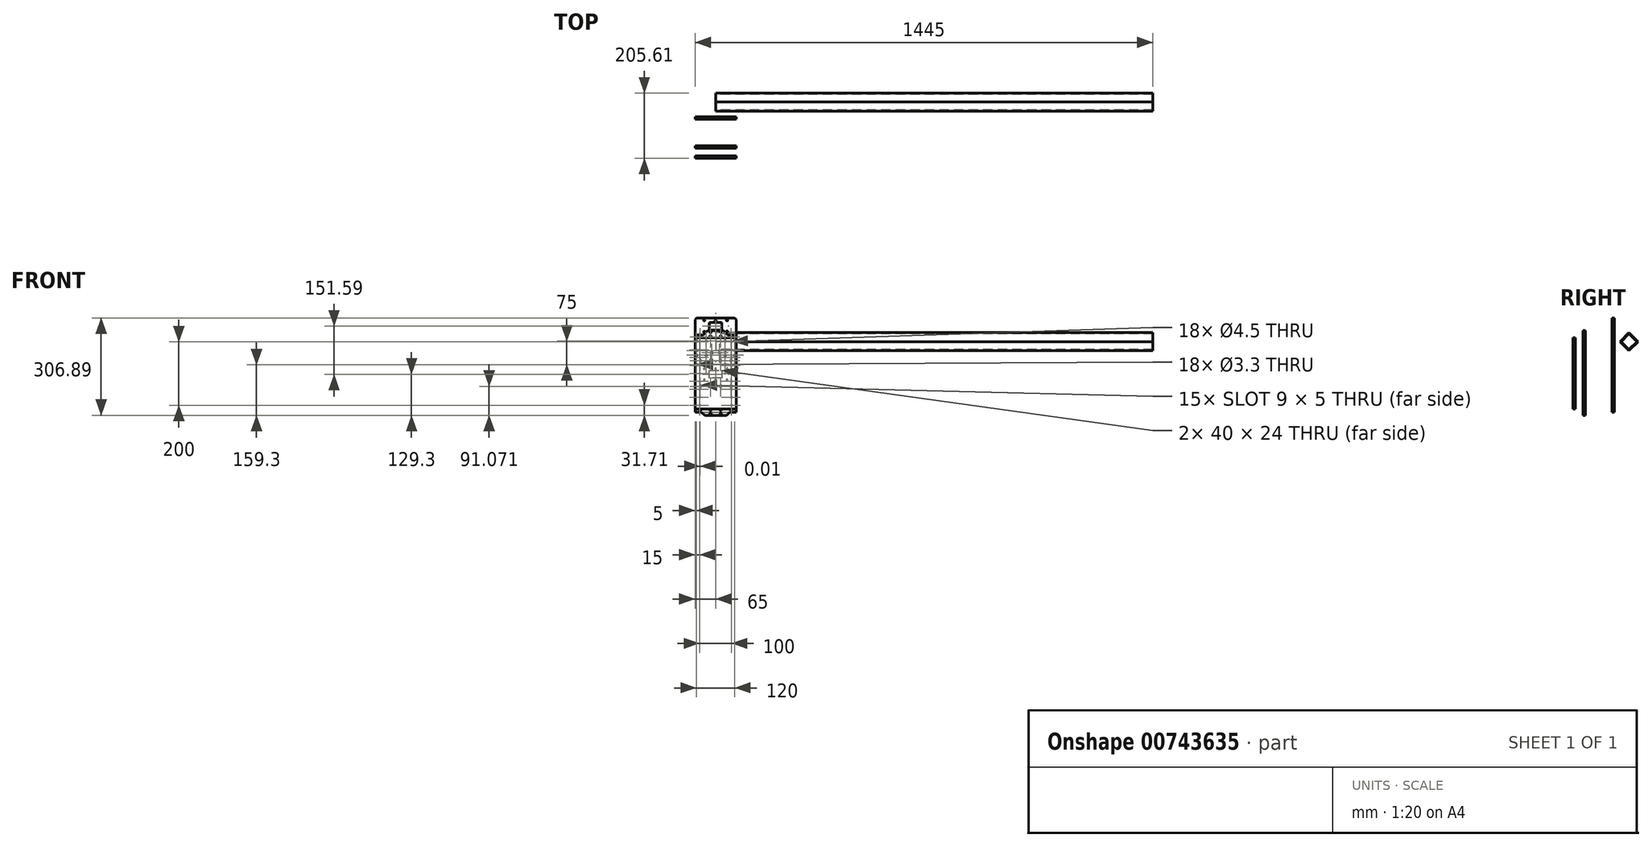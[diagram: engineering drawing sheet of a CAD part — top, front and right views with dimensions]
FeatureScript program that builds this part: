
annotation { "Feature Type Name" : "Feature", "Feature Type Description" : "" }
export const myFeature = defineFeature(function(context is Context, id is Id, definition is map)
    precondition{}
    {
        {
            var Q0;
            Q0=qCreatedBy(makeId("Front.planeOp"),FACE);
            var sketch = newSketch(context, id + "F0", { "sketchPlane" : qUnion([Q0])});
            skLineSegment(sketch, "E0", {"start": v(20, -14.5) * mm, "end": v(-20, -14.5) * mm});
            skLineSegment(sketch, "E1", {"start": v(20, 9.5) * mm, "end": v(20, -14.5) * mm});
            skLineSegment(sketch, "E2", {"start": v(-20, 9.5) * mm, "end": v(20, 9.5) * mm});
            skLineSegment(sketch, "E3", {"start": v(-20, -14.5) * mm, "end": v(-20, 9.5) * mm});
            skLineSegment(sketch, "E4", {"start": v(-51, 50.32) * mm, "end": v(-51, 47.32) * mm});
            skLineSegment(sketch, "E5", {"start": v(-46.01, 47.32) * mm, "end": v(-46.01, 50.32) * mm});
            skLineSegment(sketch, "E6", {"start": v(-18.67, 50.32) * mm, "end": v(-18.67, 47.32) * mm});
            skLineSegment(sketch, "E7", {"start": v(-13.67, 47.32) * mm, "end": v(-13.67, 50.32) * mm});
            skLineSegment(sketch, "E8", {"start": v(13.67, 50.32) * mm, "end": v(13.67, 47.32) * mm});
            skLineSegment(sketch, "E9", {"start": v(18.67, 47.32) * mm, "end": v(18.67, 50.32) * mm});
            skLineSegment(sketch, "E10", {"start": v(46, 50.32) * mm, "end": v(46, 47.32) * mm});
            skLineSegment(sketch, "E11", {"start": v(51, 47.32) * mm, "end": v(51, 50.32) * mm});
            skLineSegment(sketch, "E12", {"start": v(-51, 103.5) * mm, "end": v(-51, 100.5) * mm});
            skLineSegment(sketch, "E13", {"start": v(-46.01, 100.5) * mm, "end": v(-46.01, 103.5) * mm});
            skLineSegment(sketch, "E14", {"start": v(-13.67, 100.5) * mm, "end": v(-13.67, 103.5) * mm});
            skLineSegment(sketch, "E15", {"start": v(-18.67, 103.5) * mm, "end": v(-18.67, 100.5) * mm});
            skLineSegment(sketch, "E16", {"start": v(18.67, 100.5) * mm, "end": v(18.67, 103.5) * mm});
            skLineSegment(sketch, "E17", {"start": v(13.67, 103.5) * mm, "end": v(13.67, 100.5) * mm});
            skLineSegment(sketch, "E18", {"start": v(51, 100.5) * mm, "end": v(51, 103.5) * mm});
            skLineSegment(sketch, "E19", {"start": v(46, 103.5) * mm, "end": v(46, 100.5) * mm});
            skLineSegment(sketch, "E20", {"start": v(-46.01, -55.32) * mm, "end": v(-46.01, -52.32) * mm});
            skLineSegment(sketch, "E21", {"start": v(-51, -52.32) * mm, "end": v(-51, -55.32) * mm});
            skLineSegment(sketch, "E22", {"start": v(-13.67, -55.32) * mm, "end": v(-13.67, -52.32) * mm});
            skLineSegment(sketch, "E23", {"start": v(-18.67, -52.32) * mm, "end": v(-18.67, -55.32) * mm});
            skLineSegment(sketch, "E24", {"start": v(18.67, -55.32) * mm, "end": v(18.67, -52.32) * mm});
            skLineSegment(sketch, "E25", {"start": v(13.67, -52.32) * mm, "end": v(13.67, -55.32) * mm});
            skLineSegment(sketch, "E26", {"start": v(51, -55.32) * mm, "end": v(51, -52.32) * mm});
            skLineSegment(sketch, "E27", {"start": v(46, -52.32) * mm, "end": v(46, -55.32) * mm});
            skLineSegment(sketch, "E28", {"start": v(60, -113.5) * mm, "end": v(65, -108.5) * mm});
            skLineSegment(sketch, "E29", {"start": v(34, -124.5) * mm, "end": v(45, -113.5) * mm});
            skLineSegment(sketch, "E30", {"start": v(34, -124.5) * mm, "end": v(-34, -124.5) * mm});
            skLineSegment(sketch, "E31", {"start": v(-45, -113.5) * mm, "end": v(-34, -124.5) * mm});
            skLineSegment(sketch, "E32", {"start": v(-65, -108.5) * mm, "end": v(-60, -113.5) * mm});
            skLineSegment(sketch, "E33", {"start": v(-60, 110.5) * mm, "end": v(-65, 105.5) * mm});
            skLineSegment(sketch, "E34", {"start": v(-39, 110.5) * mm, "end": v(-60, 110.5) * mm});
            skLineSegment(sketch, "E35", {"start": v(-25, 124.5) * mm, "end": v(-39, 110.5) * mm});
            skLineSegment(sketch, "E36", {"start": v(-25, 124.5) * mm, "end": v(25, 124.5) * mm});
            skLineSegment(sketch, "E37", {"start": v(39, 110.5) * mm, "end": v(25, 124.5) * mm});
            skLineSegment(sketch, "E38", {"start": v(60, 110.5) * mm, "end": v(39, 110.5) * mm});
            skLineSegment(sketch, "E39", {"start": v(65, 105.5) * mm, "end": v(60, 110.5) * mm});
            skLineSegment(sketch, "E40", {"start": v(-65, 105.5) * mm, "end": v(-65, -108.5) * mm});
            skLineSegment(sketch, "E41", {"start": v(65, -108.5) * mm, "end": v(65, 105.5) * mm});
            skLineSegment(sketch, "E42", {"start": v(45, -113.5) * mm, "end": v(60, -113.5) * mm});
            skLineSegment(sketch, "E43", {"start": v(-60, -113.5) * mm, "end": v(-45, -113.5) * mm});
            skCircle(sketch, "E44", {"center": v(-48.5, -107) * mm, "radius": 2.5 * mm});
            skCircle(sketch, "E45", {"center": v(-16.17, -107) * mm, "radius": 2.5 * mm});
            skCircle(sketch, "E46", {"center": v(16.17, -107) * mm, "radius": 2.5 * mm});
            skCircle(sketch, "E47", {"center": v(48.5, -107) * mm, "radius": 2.5 * mm});
            skCircle(sketch, "E48", {"center": v(-36, 15) * mm, "radius": 2.05 * mm});
            skCircle(sketch, "E49", {"center": v(0, 15) * mm, "radius": 2.05 * mm});
            skCircle(sketch, "E50", {"center": v(36, 15) * mm, "radius": 2.05 * mm});
            skCircle(sketch, "E51", {"center": v(36, -20) * mm, "radius": 2.05 * mm});
            skCircle(sketch, "E52", {"center": v(0, -20) * mm, "radius": 2.05 * mm});
            skCircle(sketch, "E53", {"center": v(-36, -20) * mm, "radius": 2.05 * mm});
            skCircle(sketch, "E54", {"center": v(0, 119) * mm, "radius": 2.05 * mm});
            skCircle(sketch, "E55", {"center": v(16.17, -119.5) * mm, "radius": 2.5 * mm});
            skCircle(sketch, "E56", {"center": v(-16.17, -119.5) * mm, "radius": 2.5 * mm});
            skCircle(sketch, "E57", {"center": v(16.17, 119) * mm, "radius": 2.5 * mm});
            skCircle(sketch, "E58", {"center": v(-16.17, 119) * mm, "radius": 2.5 * mm});
            skCircle(sketch, "E59", {"center": v(50, -90) * mm, "radius": 2.25 * mm});
            skCircle(sketch, "E60", {"center": v(50, -65) * mm, "radius": 2.25 * mm});
            skCircle(sketch, "E61", {"center": v(-50, -90) * mm, "radius": 2.25 * mm});
            skCircle(sketch, "E62", {"center": v(-50, -65) * mm, "radius": 2.25 * mm});
            skCircle(sketch, "E63", {"center": v(-50, -40) * mm, "radius": 2.25 * mm});
            skCircle(sketch, "E64", {"center": v(-50, -15) * mm, "radius": 2.25 * mm});
            skCircle(sketch, "E65", {"center": v(50, -40) * mm, "radius": 2.25 * mm});
            skCircle(sketch, "E66", {"center": v(50, -15) * mm, "radius": 2.25 * mm});
            skCircle(sketch, "E67", {"center": v(50, 10) * mm, "radius": 2.25 * mm});
            skCircle(sketch, "E68", {"center": v(-50, 10) * mm, "radius": 2.25 * mm});
            skCircle(sketch, "E69", {"center": v(-50, 35) * mm, "radius": 2.25 * mm});
            skCircle(sketch, "E70", {"center": v(50, 35) * mm, "radius": 2.25 * mm});
            skCircle(sketch, "E71", {"center": v(50, 60) * mm, "radius": 2.25 * mm});
            skCircle(sketch, "E72", {"center": v(-50, 60) * mm, "radius": 2.25 * mm});
            skCircle(sketch, "E73", {"center": v(-50, 85) * mm, "radius": 2.25 * mm});
            skCircle(sketch, "E74", {"center": v(50, 85) * mm, "radius": 2.25 * mm});
            skArc(sketch, "E75", {"start": v(-51, 47.32) * mm, "mid": v(-48.5, 44.82) * mm, "end": v(-46, 47.32) * mm});
            skArc(sketch, "E76", {"start": v(-46, 50.32) * mm, "mid": v(-48.5, 52.82) * mm, "end": v(-51, 50.32) * mm});
            skArc(sketch, "E77", {"start": v(-18.67, 47.32) * mm, "mid": v(-16.17, 44.82) * mm, "end": v(-13.67, 47.32) * mm});
            skArc(sketch, "E78", {"start": v(-13.67, 50.32) * mm, "mid": v(-16.17, 52.82) * mm, "end": v(-18.67, 50.32) * mm});
            skArc(sketch, "E79", {"start": v(13.67, 47.32) * mm, "mid": v(16.17, 44.82) * mm, "end": v(18.67, 47.32) * mm});
            skArc(sketch, "E80", {"start": v(18.67, 50.32) * mm, "mid": v(16.17, 52.82) * mm, "end": v(13.67, 50.32) * mm});
            skArc(sketch, "E81", {"start": v(46, 47.32) * mm, "mid": v(48.5, 44.82) * mm, "end": v(51, 47.32) * mm});
            skArc(sketch, "E82", {"start": v(51, 50.32) * mm, "mid": v(48.5, 52.82) * mm, "end": v(46, 50.32) * mm});
            skArc(sketch, "E83", {"start": v(-51, 100.5) * mm, "mid": v(-48.5, 98) * mm, "end": v(-46, 100.5) * mm});
            skArc(sketch, "E84", {"start": v(-46, 103.5) * mm, "mid": v(-48.5, 106) * mm, "end": v(-51, 103.5) * mm});
            skArc(sketch, "E85", {"start": v(-18.67, 100.5) * mm, "mid": v(-16.17, 98) * mm, "end": v(-13.67, 100.5) * mm});
            skArc(sketch, "E86", {"start": v(-13.67, 103.5) * mm, "mid": v(-16.17, 106) * mm, "end": v(-18.67, 103.5) * mm});
            skArc(sketch, "E87", {"start": v(13.67, 100.5) * mm, "mid": v(16.17, 98) * mm, "end": v(18.67, 100.5) * mm});
            skArc(sketch, "E88", {"start": v(18.67, 103.5) * mm, "mid": v(16.17, 106) * mm, "end": v(13.67, 103.5) * mm});
            skArc(sketch, "E89", {"start": v(46, 100.5) * mm, "mid": v(48.5, 98) * mm, "end": v(51, 100.5) * mm});
            skArc(sketch, "E90", {"start": v(51, 103.5) * mm, "mid": v(48.5, 106) * mm, "end": v(46, 103.5) * mm});
            skArc(sketch, "E91", {"start": v(-51, -55.32) * mm, "mid": v(-48.5, -57.82) * mm, "end": v(-46, -55.32) * mm});
            skArc(sketch, "E92", {"start": v(-46, -52.32) * mm, "mid": v(-48.5, -49.82) * mm, "end": v(-51, -52.32) * mm});
            skArc(sketch, "E93", {"start": v(-18.67, -55.32) * mm, "mid": v(-16.17, -57.82) * mm, "end": v(-13.67, -55.32) * mm});
            skArc(sketch, "E94", {"start": v(-13.67, -52.32) * mm, "mid": v(-16.17, -49.82) * mm, "end": v(-18.67, -52.32) * mm});
            skArc(sketch, "E95", {"start": v(13.67, -55.32) * mm, "mid": v(16.17, -57.82) * mm, "end": v(18.67, -55.32) * mm});
            skArc(sketch, "E96", {"start": v(18.67, -52.32) * mm, "mid": v(16.17, -49.82) * mm, "end": v(13.67, -52.32) * mm});
            skArc(sketch, "E97", {"start": v(46, -55.32) * mm, "mid": v(48.5, -57.82) * mm, "end": v(51, -55.32) * mm});
            skArc(sketch, "E98", {"start": v(51, -52.32) * mm, "mid": v(48.5, -49.82) * mm, "end": v(46, -52.32) * mm});
            skSolve(sketch);
        }
        {
            var Q0;
            Q0=qCreatedBy(makeId("Right.planeOp"),FACE);
            var sketch = newSketch(context, id + "F1", { "sketchPlane" : qUnion([Q0])});
            skLineSegment(sketch, "E99.bottom", {"start": v(137.33, 128.79) * mm, "end": v(109.04, 100.5) * mm});
            skLineSegment(sketch, "E99.top", {"start": v(165.61, 100.5) * mm, "end": v(137.33, 72.22) * mm});
            skLineSegment(sketch, "E99.left", {"start": v(137.33, 128.79) * mm, "end": v(165.61, 100.5) * mm});
            skLineSegment(sketch, "E99.right", {"start": v(109.04, 100.5) * mm, "end": v(137.33, 72.22) * mm});
            skSolve(sketch);
        }
        {
            var Q0;
            Q0 = qSketchRegion(id + "F1", true);
            extrude(context, id + "F2", {"entities" : qUnion([Q0]), "depth" : 1380 * mm, "offsetDistance" : 25 * mm});
        }
        {
            var Q0;
            Q0=makeQuery(id+"F2.opExtrude","CAP_FACE",FACE,{"disambiguationData":[OSD([sQuery(id+"F1.wireOp",EDGE,"E99.bottom"),sQuery(id+"F1.wireOp",EDGE,"E99.top"),sQuery(id+"F1.wireOp",EDGE,"E99.left"),sQuery(id+"F1.wireOp",EDGE,"E99.right")])],"isStart":true});
            var Q1;
            Q1=makeQuery(id+"F2.opExtrude","CAP_FACE",FACE,{"disambiguationData":[OSD([sQuery(id+"F1.wireOp",EDGE,"E99.bottom"),sQuery(id+"F1.wireOp",EDGE,"E99.top"),sQuery(id+"F1.wireOp",EDGE,"E99.left"),sQuery(id+"F1.wireOp",EDGE,"E99.right")])],"isStart":false});
            shell(context, id + "F3", {"entities" : qUnion([Q0, Q1]), "thickness" : 2.5 * mm});
        }
        {
            var Q0;
            Q0=qCreatedBy(makeId("Front.planeOp"),FACE);
            var sketch = newSketch(context, id + "F4", { "sketchPlane" : qUnion([Q0])});
            skLineSegment(sketch, "E100.left", {"start": v(65, 121.7) * mm, "end": v(65, -121.7) * mm});
            skLineSegment(sketch, "E100.right", {"start": v(-65, 121.7) * mm, "end": v(-65, -121.7) * mm});
            skCircle(sketch, "E101", {"center": v(-48.5, -115.1) * mm, "radius": 2.5 * mm});
            skCircle(sketch, "E102", {"center": v(-16.18, -115.1) * mm, "radius": 2.5 * mm});
            skCircle(sketch, "E103", {"center": v(16.18, -115.1) * mm, "radius": 2.5 * mm});
            skCircle(sketch, "E104", {"center": v(48.5, -115.1) * mm, "radius": 2.5 * mm});
            skLineSegment(sketch, "E105", {"start": v(-48.5, -42.51) * mm, "end": v(-48.5, -38.51) * mm});
            skLineSegment(sketch, "E106", {"start": v(-16.18, -42.51) * mm, "end": v(-16.18, -38.51) * mm});
            skLineSegment(sketch, "E107", {"start": v(16.18, -42.51) * mm, "end": v(16.18, -38.51) * mm});
            skLineSegment(sketch, "E108", {"start": v(48.5, -42.51) * mm, "end": v(48.5, -38.51) * mm});
            skLineSegment(sketch, "E109.MirrorCS", {"start": v(16.18, 42.51) * mm, "end": v(16.18, 38.51) * mm});
            skLineSegment(sketch, "E110.MirrorCS", {"start": v(48.5, 42.51) * mm, "end": v(48.5, 38.51) * mm});
            skLineSegment(sketch, "E111.MirrorCS", {"start": v(-16.18, 42.51) * mm, "end": v(-16.18, 38.51) * mm});
            skLineSegment(sketch, "E112.MirrorCS", {"start": v(-48.5, 42.51) * mm, "end": v(-48.5, 38.51) * mm});
            skLineSegment(sketch, "E113", {"start": v(-48.5, 117.1) * mm, "end": v(-48.5, 113.1) * mm});
            skLineSegment(sketch, "E114", {"start": v(-16.18, 117.1) * mm, "end": v(-16.18, 113.1) * mm});
            skLineSegment(sketch, "E115", {"start": v(16.18, 117.1) * mm, "end": v(16.18, 113.1) * mm});
            skLineSegment(sketch, "E116", {"start": v(48.5, 117.1) * mm, "end": v(48.5, 113.1) * mm});
            skArc(sketch, "E117.0.startCap", {"start": v(-51, 117.1) * mm, "mid": v(-48.5, 119.6) * mm, "end": v(-46, 117.1) * mm});
            skArc(sketch, "E117.0.endCap", {"start": v(-46, 113.1) * mm, "mid": v(-48.5, 110.6) * mm, "end": v(-51, 113.1) * mm});
            skLineSegment(sketch, "E117.0.left", {"start": v(-46, 117.1) * mm, "end": v(-46, 113.1) * mm});
            skLineSegment(sketch, "E117.0.right", {"start": v(-51, 117.1) * mm, "end": v(-51, 113.1) * mm});
            skArc(sketch, "E117.1.startCap", {"start": v(-18.68, 117.1) * mm, "mid": v(-16.18, 119.6) * mm, "end": v(-13.68, 117.1) * mm});
            skArc(sketch, "E117.1.endCap", {"start": v(-13.68, 113.1) * mm, "mid": v(-16.18, 110.6) * mm, "end": v(-18.68, 113.1) * mm});
            skLineSegment(sketch, "E117.1.left", {"start": v(-13.68, 117.1) * mm, "end": v(-13.68, 113.1) * mm});
            skLineSegment(sketch, "E117.1.right", {"start": v(-18.68, 117.1) * mm, "end": v(-18.68, 113.1) * mm});
            skArc(sketch, "E117.2.startCap", {"start": v(13.68, 117.1) * mm, "mid": v(16.18, 119.6) * mm, "end": v(18.68, 117.1) * mm});
            skArc(sketch, "E117.2.endCap", {"start": v(18.68, 113.1) * mm, "mid": v(16.18, 110.6) * mm, "end": v(13.68, 113.1) * mm});
            skLineSegment(sketch, "E117.2.left", {"start": v(18.68, 117.1) * mm, "end": v(18.68, 113.1) * mm});
            skLineSegment(sketch, "E117.2.right", {"start": v(13.68, 117.1) * mm, "end": v(13.68, 113.1) * mm});
            skArc(sketch, "E117.3.startCap", {"start": v(46, 117.1) * mm, "mid": v(48.5, 119.6) * mm, "end": v(51, 117.1) * mm});
            skArc(sketch, "E117.3.endCap", {"start": v(51, 113.1) * mm, "mid": v(48.5, 110.6) * mm, "end": v(46, 113.1) * mm});
            skLineSegment(sketch, "E117.3.left", {"start": v(51, 117.1) * mm, "end": v(51, 113.1) * mm});
            skLineSegment(sketch, "E117.3.right", {"start": v(46, 117.1) * mm, "end": v(46, 113.1) * mm});
            skArc(sketch, "E117.4.startCap", {"start": v(-51, 42.51) * mm, "mid": v(-48.5, 45.01) * mm, "end": v(-46, 42.51) * mm});
            skArc(sketch, "E117.4.endCap", {"start": v(-46, 38.51) * mm, "mid": v(-48.5, 36.01) * mm, "end": v(-51, 38.51) * mm});
            skLineSegment(sketch, "E117.4.left", {"start": v(-46, 42.51) * mm, "end": v(-46, 38.51) * mm});
            skLineSegment(sketch, "E117.4.right", {"start": v(-51, 42.51) * mm, "end": v(-51, 38.51) * mm});
            skArc(sketch, "E117.5.startCap", {"start": v(-18.68, 42.51) * mm, "mid": v(-16.18, 45.01) * mm, "end": v(-13.68, 42.51) * mm});
            skArc(sketch, "E117.5.endCap", {"start": v(-13.68, 38.51) * mm, "mid": v(-16.18, 36.01) * mm, "end": v(-18.68, 38.51) * mm});
            skLineSegment(sketch, "E117.5.left", {"start": v(-13.68, 42.51) * mm, "end": v(-13.68, 38.51) * mm});
            skLineSegment(sketch, "E117.5.right", {"start": v(-18.68, 42.51) * mm, "end": v(-18.68, 38.51) * mm});
            skArc(sketch, "E117.6.startCap", {"start": v(13.68, 42.51) * mm, "mid": v(16.18, 45.01) * mm, "end": v(18.68, 42.51) * mm});
            skArc(sketch, "E117.6.endCap", {"start": v(18.68, 38.51) * mm, "mid": v(16.18, 36.01) * mm, "end": v(13.68, 38.51) * mm});
            skLineSegment(sketch, "E117.6.left", {"start": v(18.68, 42.51) * mm, "end": v(18.68, 38.51) * mm});
            skLineSegment(sketch, "E117.6.right", {"start": v(13.68, 42.51) * mm, "end": v(13.68, 38.51) * mm});
            skArc(sketch, "E117.7.startCap", {"start": v(46, 42.51) * mm, "mid": v(48.5, 45.01) * mm, "end": v(51, 42.51) * mm});
            skArc(sketch, "E117.7.endCap", {"start": v(51, 38.51) * mm, "mid": v(48.5, 36.01) * mm, "end": v(46, 38.51) * mm});
            skLineSegment(sketch, "E117.7.left", {"start": v(51, 42.51) * mm, "end": v(51, 38.51) * mm});
            skLineSegment(sketch, "E117.7.right", {"start": v(46, 42.51) * mm, "end": v(46, 38.51) * mm});
            skArc(sketch, "E117.8.startCap", {"start": v(51, -42.51) * mm, "mid": v(48.5, -45.01) * mm, "end": v(46, -42.51) * mm});
            skArc(sketch, "E117.8.endCap", {"start": v(46, -38.51) * mm, "mid": v(48.5, -36.01) * mm, "end": v(51, -38.51) * mm});
            skLineSegment(sketch, "E117.8.left", {"start": v(46, -42.51) * mm, "end": v(46, -38.51) * mm});
            skLineSegment(sketch, "E117.8.right", {"start": v(51, -42.51) * mm, "end": v(51, -38.51) * mm});
            skArc(sketch, "E117.9.startCap", {"start": v(18.68, -42.51) * mm, "mid": v(16.18, -45.01) * mm, "end": v(13.68, -42.51) * mm});
            skArc(sketch, "E117.9.endCap", {"start": v(13.68, -38.51) * mm, "mid": v(16.18, -36.01) * mm, "end": v(18.68, -38.51) * mm});
            skLineSegment(sketch, "E117.9.left", {"start": v(13.68, -42.51) * mm, "end": v(13.68, -38.51) * mm});
            skLineSegment(sketch, "E117.9.right", {"start": v(18.68, -42.51) * mm, "end": v(18.68, -38.51) * mm});
            skArc(sketch, "E117.10.startCap", {"start": v(-13.68, -42.51) * mm, "mid": v(-16.18, -45.01) * mm, "end": v(-18.68, -42.51) * mm});
            skArc(sketch, "E117.10.endCap", {"start": v(-18.68, -38.51) * mm, "mid": v(-16.18, -36.01) * mm, "end": v(-13.68, -38.51) * mm});
            skLineSegment(sketch, "E117.10.left", {"start": v(-18.68, -42.51) * mm, "end": v(-18.68, -38.51) * mm});
            skLineSegment(sketch, "E117.10.right", {"start": v(-13.68, -42.51) * mm, "end": v(-13.68, -38.51) * mm});
            skArc(sketch, "E117.11.startCap", {"start": v(-46, -42.51) * mm, "mid": v(-48.5, -45.01) * mm, "end": v(-51, -42.51) * mm});
            skArc(sketch, "E117.11.endCap", {"start": v(-51, -38.51) * mm, "mid": v(-48.5, -36.01) * mm, "end": v(-46, -38.51) * mm});
            skLineSegment(sketch, "E117.11.left", {"start": v(-51, -42.51) * mm, "end": v(-51, -38.51) * mm});
            skLineSegment(sketch, "E117.11.right", {"start": v(-46, -42.51) * mm, "end": v(-46, -38.51) * mm});
            skLineSegment(sketch, "E118", {"start": v(-39, 121.7) * mm, "end": v(-25, 135.7) * mm});
            skLineSegment(sketch, "E119", {"start": v(-25, 135.7) * mm, "end": v(25, 135.7) * mm});
            skLineSegment(sketch, "E120", {"start": v(25, 135.7) * mm, "end": v(39, 121.7) * mm});
            skCircle(sketch, "E121", {"center": v(-16.18, -127.6) * mm, "radius": 2.5 * mm});
            skCircle(sketch, "E122", {"center": v(16.18, -127.6) * mm, "radius": 2.5 * mm});
            skLineSegment(sketch, "E123", {"start": v(-65, -121.7) * mm, "end": v(-45, -121.7) * mm});
            skLineSegment(sketch, "E124", {"start": v(-34, -131.8) * mm, "end": v(-45, -121.7) * mm});
            skLineSegment(sketch, "E125", {"start": v(-34, -131.8) * mm, "end": v(34, -131.8) * mm});
            skLineSegment(sketch, "E126", {"start": v(34, -131.8) * mm, "end": v(45, -121.7) * mm});
            skLineSegment(sketch, "E127", {"start": v(45, -121.7) * mm, "end": v(65, -121.7) * mm});
            skCircle(sketch, "E128", {"center": v(-16.18, 130.74) * mm, "radius": 2.57 * mm});
            skCircle(sketch, "E129", {"center": v(16.18, 132.1) * mm, "radius": 2.49 * mm});
            skCircle(sketch, "E130", {"center": v(-50, -100.1) * mm, "radius": 2.25 * mm});
            skCircle(sketch, "E131.0.1.0", {"center": v(-50, -75.09) * mm, "radius": 2.25 * mm});
            skCircle(sketch, "E131.0.2.0", {"center": v(-50, -50.09) * mm, "radius": 2.25 * mm});
            skCircle(sketch, "E131.0.3.0", {"center": v(-50, -25.09) * mm, "radius": 2.25 * mm});
            skCircle(sketch, "E131.0.4.0", {"center": v(-50, -0.09) * mm, "radius": 2.25 * mm});
            skCircle(sketch, "E131.0.5.0", {"center": v(-50, 24.91) * mm, "radius": 2.25 * mm});
            skCircle(sketch, "E131.0.6.0", {"center": v(-50, 49.91) * mm, "radius": 2.25 * mm});
            skCircle(sketch, "E131.0.7.0", {"center": v(-50, 74.91) * mm, "radius": 2.25 * mm});
            skCircle(sketch, "E131.0.8.0", {"center": v(-50, 99.91) * mm, "radius": 2.25 * mm});
            skCircle(sketch, "E132.MirrorC", {"center": v(50, 49.91) * mm, "radius": 2.25 * mm});
            skCircle(sketch, "E133.MirrorC", {"center": v(50, 99.91) * mm, "radius": 2.25 * mm});
            skCircle(sketch, "E134.MirrorC", {"center": v(50, 74.91) * mm, "radius": 2.25 * mm});
            skCircle(sketch, "E135.MirrorC", {"center": v(50, 24.91) * mm, "radius": 2.25 * mm});
            skCircle(sketch, "E136.MirrorC", {"center": v(50, -25.09) * mm, "radius": 2.25 * mm});
            skCircle(sketch, "E137.MirrorC", {"center": v(50, -0.09) * mm, "radius": 2.25 * mm});
            skCircle(sketch, "E138.MirrorC", {"center": v(50, -50.09) * mm, "radius": 2.25 * mm});
            skCircle(sketch, "E139.MirrorC", {"center": v(50, -75.09) * mm, "radius": 2.25 * mm});
            skCircle(sketch, "E140.MirrorC", {"center": v(50, -100.1) * mm, "radius": 2.25 * mm});
            skLineSegment(sketch, "E141", {"start": v(-65, 121.7) * mm, "end": v(-39, 121.7) * mm});
            skLineSegment(sketch, "E142", {"start": v(39, 121.7) * mm, "end": v(65, 121.7) * mm});
            skSolve(sketch);
        }
        {
            var Q0;
            Q0=makeQuery(id+"F4.imprint","IMPRINT",FACE,{"disambiguationData":[TD([[makeQuery(id+"F4.imprint","IMPRINT",EDGE,{"derivedFrom":sQuery(id+"F4.wireOp",EDGE,"E100.bottom")}),1.0]])]});
            var Q1;
            {var subQ0=sQuery(id+"F4.wireOp",EDGE,"E118");Q1=makeQuery(id+"F4.imprint","IMPRINT",FACE,{"disambiguationData":[TD([[makeQuery(id+"F4.imprint","IMPRINT",EDGE,{"derivedFrom":subQ0}),-1.0]])]});}
            var Q2;
            {var subQ0=sQuery(id+"F4.wireOp",EDGE,"JYC6ol7t-ZKkB-sm1I-73n9-ntt4Y6ct0uzj");Q2=makeQuery(id+"F4.imprint","IMPRINT",FACE,{"disambiguationData":[TD([[makeQuery(id+"F4.imprint","IMPRINT",EDGE,{"derivedFrom":subQ0}),1.0]])]});}
            extrude(context, id + "F5", {"entities" : qUnion([Q0, Q1, Q2]), "depth" : 8 * mm, "offsetDistance" : 25 * mm});
        }
        {
            var Q0;
            Q0=qCreatedBy(makeId("Front.planeOp"),FACE);
            cPlane(context, id + "F6", {"entities" : qUnion([Q0]), "cplaneType" : CPlaneType.OFFSET, "offset" : 83 * mm, "oppositeDirection" : true, "width" : 150 * mm, "height" : 150 * mm});
        }
        {
            var Q0;
            Q0=qCreatedBy(id+"F6.planeOp",FACE);
            var sketch = newSketch(context, id + "F7", { "sketchPlane" : qUnion([Q0])});
            skLineSegment(sketch, "E143", {"start": v(-60, 175.1) * mm, "end": v(-65, 170.1) * mm});
            skLineSegment(sketch, "E144", {"start": v(60, 175.1) * mm, "end": v(-60, 175.1) * mm});
            skLineSegment(sketch, "E145", {"start": v(65, 170.1) * mm, "end": v(60, 175.1) * mm});
            skLineSegment(sketch, "E146", {"start": v(60, -121.7) * mm, "end": v(65, -116.7) * mm});
            skLineSegment(sketch, "E147", {"start": v(-65, -116.7) * mm, "end": v(-60, -121.7) * mm});
            skLineSegment(sketch, "E148", {"start": v(20, -14.5) * mm, "end": v(-20, -14.5) * mm});
            skLineSegment(sketch, "E149", {"start": v(20, 9.5) * mm, "end": v(20, -14.5) * mm});
            skLineSegment(sketch, "E150", {"start": v(-20, 9.5) * mm, "end": v(20, 9.5) * mm});
            skLineSegment(sketch, "E151", {"start": v(-20, -14.5) * mm, "end": v(-20, 9.5) * mm});
            skLineSegment(sketch, "E152", {"start": v(-51, 42.51) * mm, "end": v(-51, 38.51) * mm});
            skLineSegment(sketch, "E153", {"start": v(-46, 38.51) * mm, "end": v(-46, 42.51) * mm});
            skLineSegment(sketch, "E154", {"start": v(-18.67, 42.51) * mm, "end": v(-18.67, 38.51) * mm});
            skLineSegment(sketch, "E155", {"start": v(-13.67, 38.51) * mm, "end": v(-13.67, 42.51) * mm});
            skLineSegment(sketch, "E156", {"start": v(13.67, 42.51) * mm, "end": v(13.67, 38.51) * mm});
            skLineSegment(sketch, "E157", {"start": v(18.67, 38.51) * mm, "end": v(18.67, 42.51) * mm});
            skLineSegment(sketch, "E158", {"start": v(46, 42.51) * mm, "end": v(46, 38.51) * mm});
            skLineSegment(sketch, "E159", {"start": v(51, 38.51) * mm, "end": v(51, 42.51) * mm});
            skLineSegment(sketch, "E160", {"start": v(-51, 117.1) * mm, "end": v(-51, 113.09) * mm});
            skLineSegment(sketch, "E161", {"start": v(-46, 113.09) * mm, "end": v(-46, 117.1) * mm});
            skLineSegment(sketch, "E162", {"start": v(-13.67, 113.09) * mm, "end": v(-13.67, 117.1) * mm});
            skLineSegment(sketch, "E163", {"start": v(-18.67, 117.1) * mm, "end": v(-18.67, 113.09) * mm});
            skLineSegment(sketch, "E164", {"start": v(18.67, 113.09) * mm, "end": v(18.67, 117.1) * mm});
            skLineSegment(sketch, "E165", {"start": v(13.67, 117.1) * mm, "end": v(13.67, 113.09) * mm});
            skLineSegment(sketch, "E166", {"start": v(51, 113.09) * mm, "end": v(51, 117.1) * mm});
            skLineSegment(sketch, "E167", {"start": v(46, 117.1) * mm, "end": v(46, 113.1) * mm});
            skLineSegment(sketch, "E168", {"start": v(-46, -42.73) * mm, "end": v(-46, -38.73) * mm});
            skLineSegment(sketch, "E169", {"start": v(-51, -38.73) * mm, "end": v(-51, -42.73) * mm});
            skLineSegment(sketch, "E170", {"start": v(-13.67, -42.73) * mm, "end": v(-13.67, -38.73) * mm});
            skLineSegment(sketch, "E171", {"start": v(-18.67, -38.73) * mm, "end": v(-18.67, -42.73) * mm});
            skLineSegment(sketch, "E172", {"start": v(18.67, -42.73) * mm, "end": v(18.67, -38.73) * mm});
            skLineSegment(sketch, "E173", {"start": v(13.67, -38.73) * mm, "end": v(13.67, -42.73) * mm});
            skLineSegment(sketch, "E174", {"start": v(51, -42.73) * mm, "end": v(51, -38.73) * mm});
            skLineSegment(sketch, "E175", {"start": v(46, -38.73) * mm, "end": v(46, -42.73) * mm});
            skLineSegment(sketch, "E176", {"start": v(20, 161.1) * mm, "end": v(-20, 161.1) * mm});
            skLineSegment(sketch, "E177", {"start": v(-20, 161.1) * mm, "end": v(-20, 137.1) * mm});
            skLineSegment(sketch, "E178", {"start": v(-20, 137.1) * mm, "end": v(20, 137.1) * mm});
            skLineSegment(sketch, "E179", {"start": v(20, 137.1) * mm, "end": v(20, 161.09) * mm});
            skLineSegment(sketch, "E180", {"start": v(-65, 170.1) * mm, "end": v(-65, -116.7) * mm});
            skLineSegment(sketch, "E181", {"start": v(65, -116.7) * mm, "end": v(65, 170.09) * mm});
            skLineSegment(sketch, "E182", {"start": v(-60, -121.7) * mm, "end": v(60, -121.7) * mm});
            skCircle(sketch, "E183", {"center": v(-48.5, -115.2) * mm, "radius": 2.5 * mm});
            skCircle(sketch, "E184", {"center": v(-16.17, -115.2) * mm, "radius": 2.5 * mm});
            skCircle(sketch, "E185", {"center": v(16.17, -115.2) * mm, "radius": 2.5 * mm});
            skCircle(sketch, "E186", {"center": v(48.5, -115.2) * mm, "radius": 2.5 * mm});
            skCircle(sketch, "E187", {"center": v(-36, 15) * mm, "radius": 2.05 * mm});
            skCircle(sketch, "E188", {"center": v(0, 15) * mm, "radius": 2.05 * mm});
            skCircle(sketch, "E189", {"center": v(36, 15) * mm, "radius": 2.05 * mm});
            skCircle(sketch, "E190", {"center": v(36, -20) * mm, "radius": 2.05 * mm});
            skCircle(sketch, "E191", {"center": v(0, -20) * mm, "radius": 2.05 * mm});
            skCircle(sketch, "E192", {"center": v(-36, -20) * mm, "radius": 2.05 * mm});
            skCircle(sketch, "E193", {"center": v(-36, 167.6) * mm, "radius": 2.05 * mm});
            skCircle(sketch, "E194", {"center": v(0, 166.6) * mm, "radius": 2.05 * mm});
            skCircle(sketch, "E195", {"center": v(36, 167.6) * mm, "radius": 2.05 * mm});
            skCircle(sketch, "E196", {"center": v(36, 132.6) * mm, "radius": 2.05 * mm});
            skCircle(sketch, "E197", {"center": v(0, 131.59) * mm, "radius": 2.05 * mm});
            skCircle(sketch, "E198", {"center": v(-36, 131.59) * mm, "radius": 2.05 * mm});
            skArc(sketch, "E199", {"start": v(-51, 38.51) * mm, "mid": v(-48.5, 36.01) * mm, "end": v(-46, 38.51) * mm});
            skArc(sketch, "E200", {"start": v(-45.97, 42.51) * mm, "mid": v(-48.47, 45.01) * mm, "end": v(-50.97, 42.51) * mm});
            skArc(sketch, "E201", {"start": v(-18.67, 38.51) * mm, "mid": v(-16.17, 36.01) * mm, "end": v(-13.67, 38.51) * mm});
            skArc(sketch, "E202", {"start": v(-13.64, 42.51) * mm, "mid": v(-16.14, 45.01) * mm, "end": v(-18.64, 42.51) * mm});
            skArc(sketch, "E203", {"start": v(13.67, 38.51) * mm, "mid": v(16.17, 36.01) * mm, "end": v(18.67, 38.51) * mm});
            skArc(sketch, "E204", {"start": v(18.7, 42.51) * mm, "mid": v(16.2, 45.01) * mm, "end": v(13.7, 42.51) * mm});
            skArc(sketch, "E205", {"start": v(46.01, 38.51) * mm, "mid": v(48.51, 36.01) * mm, "end": v(51, 38.51) * mm});
            skArc(sketch, "E206", {"start": v(51.05, 42.51) * mm, "mid": v(48.55, 45.01) * mm, "end": v(46.05, 42.51) * mm});
            skArc(sketch, "E207", {"start": v(-51, 113.1) * mm, "mid": v(-48.5, 110.6) * mm, "end": v(-46, 113.1) * mm});
            skArc(sketch, "E208", {"start": v(-46, 117.1) * mm, "mid": v(-48.5, 119.6) * mm, "end": v(-51, 117.1) * mm});
            skArc(sketch, "E209", {"start": v(-18.67, 113.1) * mm, "mid": v(-16.17, 110.6) * mm, "end": v(-13.67, 113.1) * mm});
            skArc(sketch, "E210", {"start": v(-13.67, 117.1) * mm, "mid": v(-16.17, 119.6) * mm, "end": v(-18.67, 117.1) * mm});
            skArc(sketch, "E211", {"start": v(13.68, 113.1) * mm, "mid": v(16.18, 110.6) * mm, "end": v(18.68, 113.1) * mm});
            skArc(sketch, "E212", {"start": v(18.65, 117.1) * mm, "mid": v(16.15, 119.6) * mm, "end": v(13.65, 117.1) * mm});
            skArc(sketch, "E213", {"start": v(46, 113.1) * mm, "mid": v(48.5, 110.6) * mm, "end": v(51, 113.1) * mm});
            skArc(sketch, "E214", {"start": v(51, 117.1) * mm, "mid": v(48.5, 119.6) * mm, "end": v(46, 117.1) * mm});
            skArc(sketch, "E215", {"start": v(-51, -42.73) * mm, "mid": v(-48.5, -45.23) * mm, "end": v(-46, -42.73) * mm});
            skArc(sketch, "E216", {"start": v(-46.02, -38.73) * mm, "mid": v(-48.52, -36.23) * mm, "end": v(-51.02, -38.73) * mm});
            skArc(sketch, "E217", {"start": v(-18.67, -42.73) * mm, "mid": v(-16.17, -45.23) * mm, "end": v(-13.67, -42.73) * mm});
            skArc(sketch, "E218", {"start": v(-13.68, -38.73) * mm, "mid": v(-16.18, -36.23) * mm, "end": v(-18.68, -38.73) * mm});
            skArc(sketch, "E219", {"start": v(13.67, -42.73) * mm, "mid": v(16.17, -45.23) * mm, "end": v(18.67, -42.73) * mm});
            skArc(sketch, "E220", {"start": v(18.65, -38.73) * mm, "mid": v(16.15, -36.23) * mm, "end": v(13.65, -38.73) * mm});
            skArc(sketch, "E221", {"start": v(45.97, -42.73) * mm, "mid": v(48.47, -45.23) * mm, "end": v(50.97, -42.73) * mm});
            skArc(sketch, "E222", {"start": v(51, -38.73) * mm, "mid": v(48.5, -36.23) * mm, "end": v(46, -38.73) * mm});
            skLineSegment(sketch, "E223.bottom", {"start": v(46, 117.1) * mm, "end": v(51, 117.1) * mm});
            skLineSegment(sketch, "E223.top", {"start": v(46, 113.1) * mm, "end": v(51, 113.1) * mm});
            skLineSegment(sketch, "E223.right", {"start": v(51, 117.1) * mm, "end": v(51, 113.1) * mm});
            skLineSegment(sketch, "E224.bottom", {"start": v(13.67, 117.1) * mm, "end": v(18.68, 117.1) * mm});
            skLineSegment(sketch, "E224.top", {"start": v(13.67, 113.1) * mm, "end": v(18.68, 113.1) * mm});
            skLineSegment(sketch, "E224.left", {"start": v(13.67, 117.1) * mm, "end": v(13.67, 113.1) * mm});
            skLineSegment(sketch, "E224.right", {"start": v(18.68, 117.1) * mm, "end": v(18.68, 113.1) * mm});
            skLineSegment(sketch, "E225.bottom", {"start": v(-18.67, 117.1) * mm, "end": v(-13.67, 117.1) * mm});
            skLineSegment(sketch, "E225.top", {"start": v(-18.67, 113.1) * mm, "end": v(-13.67, 113.1) * mm});
            skLineSegment(sketch, "E225.left", {"start": v(-18.67, 117.1) * mm, "end": v(-18.67, 113.1) * mm});
            skLineSegment(sketch, "E225.right", {"start": v(-13.67, 117.1) * mm, "end": v(-13.67, 113.1) * mm});
            skLineSegment(sketch, "E226.bottom", {"start": v(-51, 117.1) * mm, "end": v(-46, 117.1) * mm});
            skLineSegment(sketch, "E226.top", {"start": v(-51, 113.1) * mm, "end": v(-46, 113.1) * mm});
            skLineSegment(sketch, "E226.left", {"start": v(-51, 117.1) * mm, "end": v(-51, 113.1) * mm});
            skLineSegment(sketch, "E226.right", {"start": v(-46, 117.1) * mm, "end": v(-46, 113.1) * mm});
            skCircle(sketch, "E227", {"center": v(-48.5, 117.1) * mm, "radius": 2.5 * mm});
            skCircle(sketch, "E228", {"center": v(-48.5, 113.1) * mm, "radius": 2.5 * mm});
            skCircle(sketch, "E229", {"center": v(-16.17, 117.1) * mm, "radius": 2.5 * mm});
            skCircle(sketch, "E230", {"center": v(-16.17, 113.1) * mm, "radius": 2.5 * mm});
            skCircle(sketch, "E231", {"center": v(16.15, 117.1) * mm, "radius": 2.5 * mm});
            skCircle(sketch, "E232", {"center": v(16.18, 113.1) * mm, "radius": 2.5 * mm});
            skCircle(sketch, "E233", {"center": v(48.5, 117.1) * mm, "radius": 2.5 * mm});
            skCircle(sketch, "E234", {"center": v(48.5, 113.1) * mm, "radius": 2.5 * mm});
            skLineSegment(sketch, "E235.bottom", {"start": v(-50.97, 42.51) * mm, "end": v(-46, 42.51) * mm});
            skLineSegment(sketch, "E235.top", {"start": v(-50.97, 38.51) * mm, "end": v(-46, 38.51) * mm});
            skLineSegment(sketch, "E235.left", {"start": v(-50.97, 42.51) * mm, "end": v(-50.97, 38.51) * mm});
            skLineSegment(sketch, "E235.right", {"start": v(-46, 42.51) * mm, "end": v(-46, 38.51) * mm});
            skLineSegment(sketch, "E236.bottom", {"start": v(-18.64, 42.51) * mm, "end": v(-13.67, 42.51) * mm});
            skLineSegment(sketch, "E236.top", {"start": v(-18.64, 38.51) * mm, "end": v(-13.67, 38.51) * mm});
            skLineSegment(sketch, "E236.left", {"start": v(-18.64, 42.51) * mm, "end": v(-18.64, 38.51) * mm});
            skLineSegment(sketch, "E236.right", {"start": v(-13.67, 42.51) * mm, "end": v(-13.67, 38.51) * mm});
            skLineSegment(sketch, "E237.bottom", {"start": v(13.7, 42.51) * mm, "end": v(18.67, 42.51) * mm});
            skLineSegment(sketch, "E237.top", {"start": v(13.7, 38.51) * mm, "end": v(18.67, 38.51) * mm});
            skLineSegment(sketch, "E237.left", {"start": v(13.7, 42.51) * mm, "end": v(13.7, 38.51) * mm});
            skLineSegment(sketch, "E237.right", {"start": v(18.67, 42.51) * mm, "end": v(18.67, 38.51) * mm});
            skLineSegment(sketch, "E238.bottom", {"start": v(46.05, 42.51) * mm, "end": v(51, 42.51) * mm});
            skLineSegment(sketch, "E238.top", {"start": v(46.05, 38.51) * mm, "end": v(51, 38.51) * mm});
            skLineSegment(sketch, "E238.left", {"start": v(46.05, 42.51) * mm, "end": v(46.05, 38.51) * mm});
            skLineSegment(sketch, "E238.right", {"start": v(51, 42.51) * mm, "end": v(51, 38.51) * mm});
            skCircle(sketch, "E239", {"center": v(-48.47, 42.51) * mm, "radius": 2.5 * mm});
            skCircle(sketch, "E240", {"center": v(-48.5, 38.51) * mm, "radius": 2.5 * mm});
            skCircle(sketch, "E241", {"center": v(-16.14, 42.51) * mm, "radius": 2.5 * mm});
            skCircle(sketch, "E242", {"center": v(-16.17, 38.51) * mm, "radius": 2.5 * mm});
            skCircle(sketch, "E243", {"center": v(16.2, 42.51) * mm, "radius": 2.5 * mm});
            skCircle(sketch, "E244", {"center": v(16.17, 38.51) * mm, "radius": 2.5 * mm});
            skCircle(sketch, "E245", {"center": v(48.55, 42.51) * mm, "radius": 2.5 * mm});
            skCircle(sketch, "E246", {"center": v(48.51, 38.51) * mm, "radius": 2.5 * mm});
            skCircle(sketch, "E247", {"center": v(48.5, -38.73) * mm, "radius": 2.5 * mm});
            skCircle(sketch, "E248", {"center": v(48.47, -42.73) * mm, "radius": 2.54 * mm});
            skCircle(sketch, "E249", {"center": v(16.17, -42.73) * mm, "radius": 2.5 * mm});
            skCircle(sketch, "E250", {"center": v(16.15, -38.73) * mm, "radius": 2.5 * mm});
            skCircle(sketch, "E251", {"center": v(-16.18, -38.73) * mm, "radius": 2.5 * mm});
            skCircle(sketch, "E252", {"center": v(-16.17, -42.73) * mm, "radius": 2.5 * mm});
            skCircle(sketch, "E253", {"center": v(-48.52, -38.73) * mm, "radius": 2.5 * mm});
            skCircle(sketch, "E254", {"center": v(-48.5, -42.73) * mm, "radius": 2.5 * mm});
            skLineSegment(sketch, "E255.bottom", {"start": v(-51, -38.73) * mm, "end": v(-46, -38.73) * mm});
            skLineSegment(sketch, "E255.top", {"start": v(-51, -42.73) * mm, "end": v(-46, -42.73) * mm});
            skLineSegment(sketch, "E255.right", {"start": v(-46, -38.73) * mm, "end": v(-46, -42.73) * mm});
            skLineSegment(sketch, "E256.bottom", {"start": v(-18.67, -38.73) * mm, "end": v(-13.67, -38.73) * mm});
            skLineSegment(sketch, "E256.top", {"start": v(-18.67, -42.73) * mm, "end": v(-13.67, -42.73) * mm});
            skLineSegment(sketch, "E256.right", {"start": v(-13.67, -38.73) * mm, "end": v(-13.67, -42.73) * mm});
            skLineSegment(sketch, "E257.bottom", {"start": v(13.67, -38.73) * mm, "end": v(18.67, -38.73) * mm});
            skLineSegment(sketch, "E257.top", {"start": v(13.67, -42.73) * mm, "end": v(18.67, -42.73) * mm});
            skLineSegment(sketch, "E257.right", {"start": v(18.67, -38.73) * mm, "end": v(18.67, -42.73) * mm});
            skLineSegment(sketch, "E258.bottom", {"start": v(46, -38.73) * mm, "end": v(51, -38.73) * mm});
            skLineSegment(sketch, "E258.top", {"start": v(46, -42.73) * mm, "end": v(51, -42.73) * mm});
            skLineSegment(sketch, "E258.right", {"start": v(51, -38.73) * mm, "end": v(51, -42.73) * mm});
            skSolve(sketch);
        }
        {
            var Q0;
            Q0 = qSketchRegion(id + "F7", true);
            extrude(context, id + "F8", {"entities" : qUnion([Q0]), "oppositeDirection" : true, "depth" : 8 * mm, "offsetDistance" : 25 * mm});
        }
        {
            var Q0;
            Q0=qCreatedBy(makeId("Front.planeOp"),FACE);
            cPlane(context, id + "F9", {"entities" : qUnion([Q0]), "cplaneType" : CPlaneType.OFFSET, "offset" : 32 * mm, "width" : 150 * mm, "height" : 150 * mm});
        }
        {
            var Q0;
            Q0=qCreatedBy(id+"F9.planeOp",FACE);
            var sketch = newSketch(context, id + "F10", { "sketchPlane" : qUnion([Q0])});
            skLineSegment(sketch, "E259.bottom", {"start": v(-65, -112.5) * mm, "end": v(65, -112.5) * mm});
            skLineSegment(sketch, "E259.top", {"start": v(-65, 112.5) * mm, "end": v(65, 112.5) * mm});
            skLineSegment(sketch, "E259.left", {"start": v(-65, -112.5) * mm, "end": v(-65, 112.5) * mm});
            skLineSegment(sketch, "E259.right", {"start": v(65, -112.5) * mm, "end": v(65, 112.5) * mm});
            skPoint(sketch, "E259.middle", {"position": v(0, 0) * mm});
            skCircle(sketch, "E260", {"center": v(-60, 102.5) * mm, "radius": 1.65 * mm});
            skCircle(sketch, "E261", {"center": v(-30, 102.5) * mm, "radius": 1.65 * mm});
            skCircle(sketch, "E262", {"center": v(-30, 72.5) * mm, "radius": 1.65 * mm});
            skCircle(sketch, "E263", {"center": v(-60, 72.5) * mm, "radius": 1.65 * mm});
            skCircle(sketch, "E264.0.1.0", {"center": v(-60, 57.5) * mm, "radius": 1.65 * mm});
            skCircle(sketch, "E264.0.1.1", {"center": v(-30, 27.5) * mm, "radius": 1.65 * mm});
            skCircle(sketch, "E264.0.1.2", {"center": v(-60, 27.5) * mm, "radius": 1.65 * mm});
            skCircle(sketch, "E264.0.1.3", {"center": v(-30, 57.5) * mm, "radius": 1.65 * mm});
            skLineSegment(sketch, "E264.direction1", {"start": v(-60, 72.5) * mm, "end": v(-35.5, 72.5) * mm, "construction": true});
            skLineSegment(sketch, "E264.direction2", {"start": v(-60, 72.5) * mm, "end": v(-60, 27.5) * mm, "construction": true});
            skCircle(sketch, "E265.MirrorC", {"center": v(60, 72.5) * mm, "radius": 1.65 * mm});
            skCircle(sketch, "E266.MirrorC", {"center": v(60, 27.5) * mm, "radius": 1.65 * mm});
            skCircle(sketch, "E267.MirrorC", {"center": v(30, 72.5) * mm, "radius": 1.65 * mm});
            skCircle(sketch, "E268.MirrorC", {"center": v(30, 102.5) * mm, "radius": 1.65 * mm});
            skCircle(sketch, "E269.MirrorC", {"center": v(60, 102.5) * mm, "radius": 1.65 * mm});
            skCircle(sketch, "E270.MirrorC", {"center": v(30, 27.5) * mm, "radius": 1.65 * mm});
            skCircle(sketch, "E271.MirrorC", {"center": v(60, 57.5) * mm, "radius": 1.65 * mm});
            skCircle(sketch, "E272.MirrorC", {"center": v(30, 57.5) * mm, "radius": 1.65 * mm});
            skLineSegment(sketch, "E273.MirrorCS", {"start": v(60, 72.5) * mm, "end": v(35.5, 72.5) * mm, "construction": true});
            skLineSegment(sketch, "E274.MirrorCS", {"start": v(60, 72.5) * mm, "end": v(60, 27.5) * mm, "construction": true});
            skCircle(sketch, "E275", {"center": v(-12, 65.5) * mm, "radius": 1.65 * mm});
            skCircle(sketch, "E276.MirrorC", {"center": v(12, 65.5) * mm, "radius": 1.65 * mm});
            skSolve(sketch);
        }
        {
            var Q0;
            Q0=makeQuery(id+"F10.imprint","IMPRINT",FACE,{"disambiguationData":[TD([[makeQuery(id+"F10.imprint","IMPRINT",EDGE,{"derivedFrom":sQuery(id+"F10.wireOp",EDGE,"E259.bottom")}),1.0]])]});
            extrude(context, id + "F11", {"entities" : qUnion([Q0]), "depth" : 8 * mm, "offsetDistance" : 25 * mm});
        }
    });
